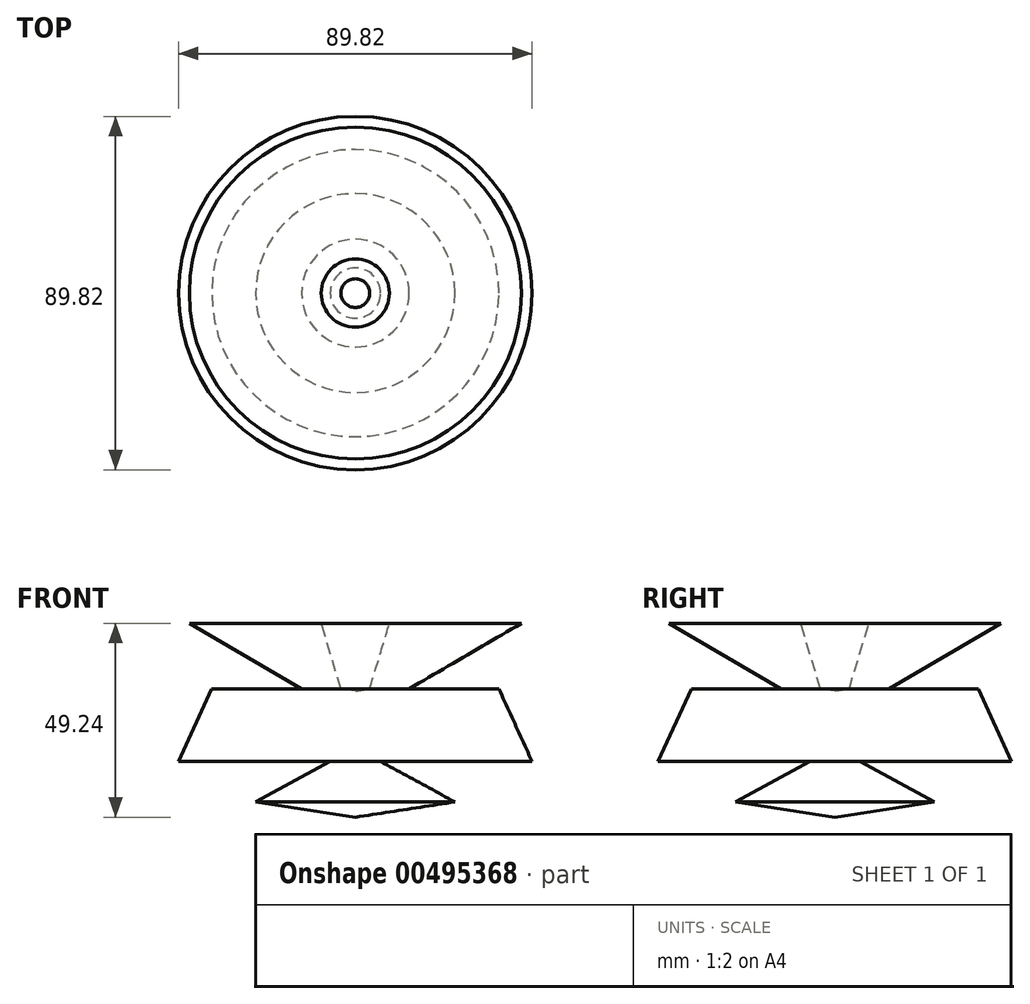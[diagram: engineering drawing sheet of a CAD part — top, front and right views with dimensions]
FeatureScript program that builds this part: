
annotation { "Feature Type Name" : "Feature", "Feature Type Description" : "" }
export const myFeature = defineFeature(function(context is Context, id is Id, definition is map)
    precondition{}
    {
        {
            var Q0;
            Q0=qCreatedBy(makeId("Front.planeOp"),FACE);
            var sketch = newSketch(context, id + "F0", { "sketchPlane" : qUnion([Q0])});
            skLineSegment(sketch, "E0", {"start": v(0, 0) * mm, "end": v(25.3, 3.88) * mm});
            skLineSegment(sketch, "E1", {"start": v(25.3, 3.88) * mm, "end": v(6.38, 14.13) * mm});
            skLineSegment(sketch, "E2", {"start": v(6.38, 14.13) * mm, "end": v(44.9, 14.13) * mm});
            skLineSegment(sketch, "E3", {"start": v(44.9, 14.13) * mm, "end": v(36.47, 32.6) * mm});
            skLineSegment(sketch, "E4", {"start": v(36.47, 32.6) * mm, "end": v(13.68, 32.6) * mm});
            skLineSegment(sketch, "E5", {"start": v(13.68, 32.6) * mm, "end": v(42.17, 49.24) * mm});
            skLineSegment(sketch, "E6", {"start": v(42.17, 49.24) * mm, "end": v(8.66, 49.24) * mm});
            skLineSegment(sketch, "E7", {"start": v(8.66, 49.24) * mm, "end": v(3.65, 32.6) * mm});
            skLineSegment(sketch, "E8", {"start": v(3.65, 32.6) * mm, "end": v(0, 32.04) * mm});
            skLineSegment(sketch, "E9", {"start": v(0, 32.04) * mm, "end": v(0, 0) * mm});
            skSolve(sketch);
        }
        {
            var Q0;
            Q0=makeQuery(id+"F0.imprint","IMPRINT",FACE,{"disambiguationData":[TD([[makeQuery(id+"F0.imprint","IMPRINT",EDGE,{"derivedFrom":sQuery(id+"F0.wireOp",EDGE,"E0")}),1.0]])]});
            var Q1;
            Q1=sQuery(id+"F0.wireOp",EDGE,"E9");
            revolve(context, id + "F1", {"entities" : qUnion([Q0]), "axis" : qUnion([Q1]), "revolveType" : RevolveType.FULL});
        }
    });
